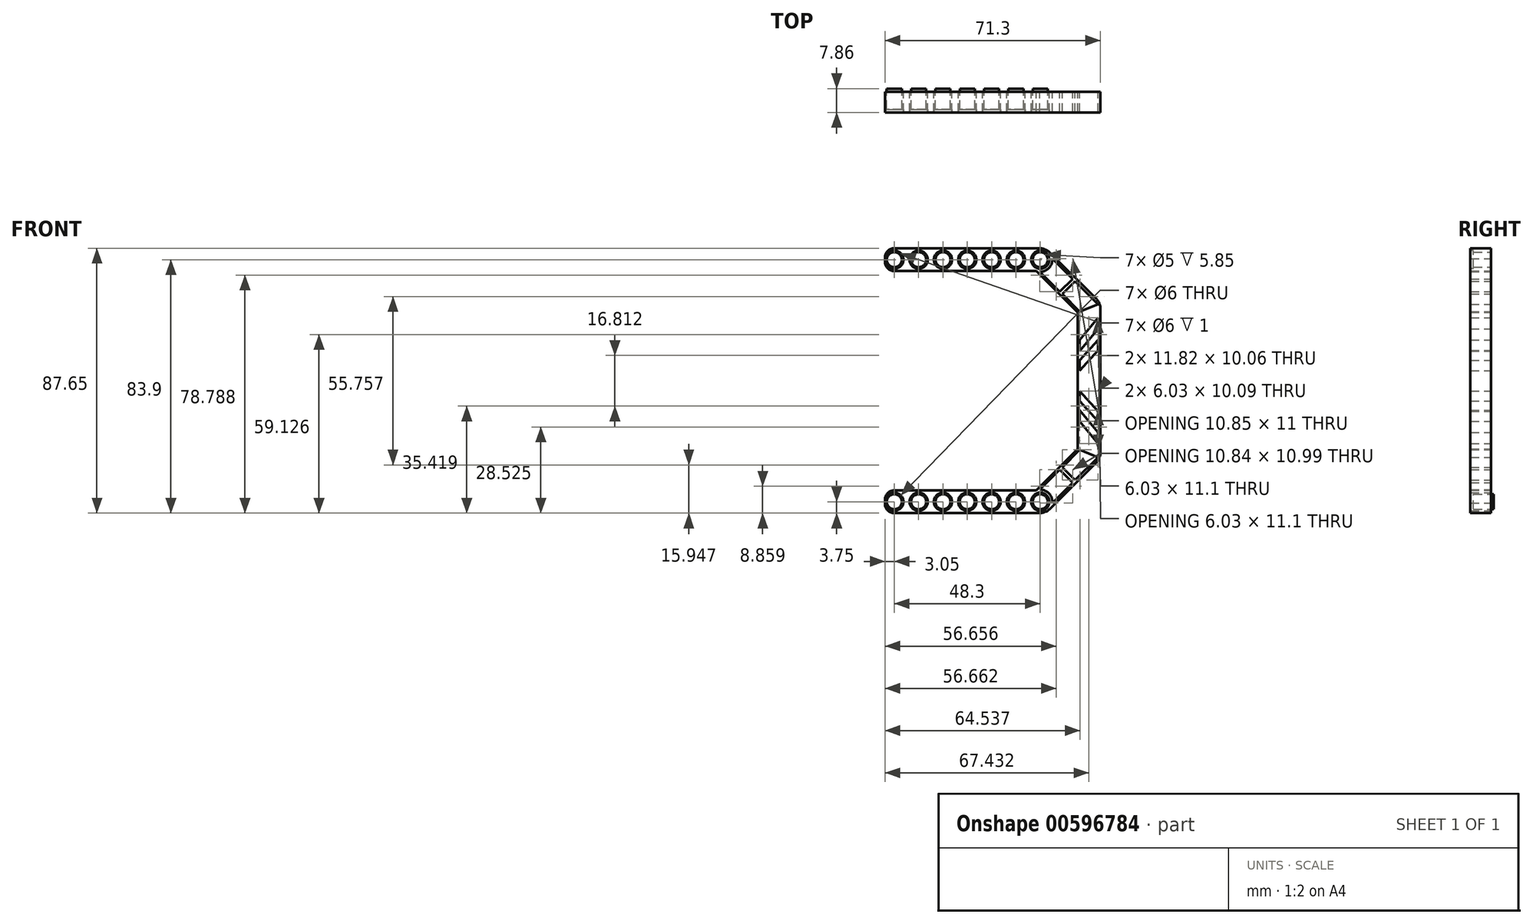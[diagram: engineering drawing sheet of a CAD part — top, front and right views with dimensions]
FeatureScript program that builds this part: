
annotation { "Feature Type Name" : "Feature", "Feature Type Description" : "" }
export const myFeature = defineFeature(function(context is Context, id is Id, definition is map)
    precondition{}
    {
        {
            var Q0;
            Q0=qCreatedBy(makeId("Front.planeOp"),FACE);
            var sketch = newSketch(context, id + "F0", { "sketchPlane" : qUnion([Q0])});
            skLineSegment(sketch, "E0.bottom", {"start": v(17.53, 19.75) * mm, "end": v(-35.65, 19.75) * mm});
            skLineSegment(sketch, "E0.right", {"start": v(-35.65, 19.75) * mm, "end": v(-35.65, 12.25) * mm});
            skPoint(sketch, "E0.middle", {"position": v(0, 0) * mm});
            skPoint(sketch, "E1.end.orphan", {"position": v(0, 37.73) * mm});
            skPoint(sketch, "E2.start.orphan", {"position": v(14.4, 19.75) * mm});
            skPoint(sketch, "E3.start.orphan", {"position": v(35.65, -1.5) * mm});
            skLineSegment(sketch, "E4", {"start": v(-35.65, 12.25) * mm, "end": v(14.4, 12.25) * mm});
            skLineSegment(sketch, "E5", {"start": v(-35.65, 19.75) * mm, "end": v(17.53, 19.75) * mm});
            skLineSegment(sketch, "E6", {"start": v(14.4, 12.25) * mm, "end": v(28.1, -1.5) * mm});
            skLineSegment(sketch, "E7", {"start": v(17.53, 19.75) * mm, "end": v(35.65, 1.63) * mm});
            skLineSegment(sketch, "E8.trimOffspring", {"start": v(28.1, -1.5) * mm, "end": v(28.15, -19.75) * mm});
            skPoint(sketch, "E9.start.orphan", {"position": v(21.25, 5.37) * mm});
            skPoint(sketch, "E10.trimOffspring.end.orphan", {"position": v(28.15, 12.2) * mm});
            skCircle(sketch, "E11", {"center": v(-16.5, 16) * mm, "radius": 2.5 * mm});
            skCircle(sketch, "E12", {"center": v(-24.55, 16) * mm, "radius": 2.5 * mm});
            skCircle(sketch, "E13", {"center": v(-32.6, 16) * mm, "radius": 2.5 * mm});
            skCircle(sketch, "E14", {"center": v(-8.45, 16) * mm, "radius": 2.5 * mm});
            skCircle(sketch, "E15", {"center": v(-0.4, 16) * mm, "radius": 2.5 * mm});
            skCircle(sketch, "E16", {"center": v(7.65, 16) * mm, "radius": 2.5 * mm});
            skCircle(sketch, "E17", {"center": v(15.7, 16) * mm, "radius": 2.5 * mm});
            skCircle(sketch, "E18", {"center": v(-32.6, 16) * mm, "radius": 3 * mm});
            skCircle(sketch, "E19", {"center": v(-24.55, 16) * mm, "radius": 3 * mm});
            skCircle(sketch, "E20", {"center": v(-16.5, 16) * mm, "radius": 3 * mm});
            skCircle(sketch, "E21", {"center": v(-8.45, 16) * mm, "radius": 3 * mm});
            skCircle(sketch, "E22", {"center": v(-0.4, 16) * mm, "radius": 3 * mm});
            skCircle(sketch, "E23", {"center": v(7.65, 16) * mm, "radius": 3 * mm});
            skCircle(sketch, "E24", {"center": v(15.7, 16) * mm, "radius": 3 * mm});
            skPoint(sketch, "E25.orphan", {"position": v(-35.65, -19.75) * mm});
            skLineSegment(sketch, "E26.trimOffspring", {"start": v(35.65, 1.63) * mm, "end": v(35.65, -19.75) * mm});
            skLineSegment(sketch, "E27.left", {"start": v(28.15, -19.75) * mm, "end": v(28.15, -28.4) * mm});
            skLineSegment(sketch, "E27.right", {"start": v(35.65, -19.75) * mm, "end": v(35.65, -28.4) * mm});
            skPoint(sketch, "E28.startSnap0", {"position": v(35.65, -24.07) * mm});
            skCircle(sketch, "E29.MirrorC", {"center": v(15.7, -64.15) * mm, "radius": 2.5 * mm});
            skLineSegment(sketch, "E30.MirrorCS", {"start": v(35.65, -67.9) * mm, "end": v(35.65, -66.58) * mm});
            skCircle(sketch, "E31.MirrorC", {"center": v(-0.4, -64.15) * mm, "radius": 2.5 * mm});
            skLineSegment(sketch, "E32.MirrorCS", {"start": v(-35.65, -67.9) * mm, "end": v(-35.65, -60.4) * mm});
            skCircle(sketch, "E33.MirrorC", {"center": v(-16.5, -64.15) * mm, "radius": 2.5 * mm});
            skLineSegment(sketch, "E34.MirrorCS", {"start": v(17.53, -67.9) * mm, "end": v(-35.65, -67.9) * mm});
            skPoint(sketch, "E35.MirrorP", {"position": v(-35.65, -28.4) * mm});
            skCircle(sketch, "E36.MirrorC", {"center": v(-8.45, -64.15) * mm, "radius": 2.5 * mm});
            skCircle(sketch, "E37.MirrorC", {"center": v(-24.55, -64.15) * mm, "radius": 2.5 * mm});
            skCircle(sketch, "E38.MirrorC", {"center": v(7.65, -64.15) * mm, "radius": 2.5 * mm});
            skCircle(sketch, "E39.MirrorC", {"center": v(-32.6, -64.15) * mm, "radius": 2.5 * mm});
            skCircle(sketch, "E40.MirrorC", {"center": v(-0.4, -64.15) * mm, "radius": 3 * mm});
            skPoint(sketch, "E41.MirrorP", {"position": v(21.25, -53.52) * mm});
            skCircle(sketch, "E42.MirrorC", {"center": v(-16.5, -64.15) * mm, "radius": 3 * mm});
            skCircle(sketch, "E43.MirrorC", {"center": v(-8.45, -64.15) * mm, "radius": 3 * mm});
            skCircle(sketch, "E44.MirrorC", {"center": v(7.65, -64.15) * mm, "radius": 3 * mm});
            skLineSegment(sketch, "E45.MirrorCS", {"start": v(28.1, -46.65) * mm, "end": v(28.15, -28.4) * mm});
            skCircle(sketch, "E46.MirrorC", {"center": v(-32.6, -64.15) * mm, "radius": 3 * mm});
            skLineSegment(sketch, "E47.MirrorCS", {"start": v(-35.65, -67.9) * mm, "end": v(17.53, -67.9) * mm});
            skLineSegment(sketch, "E48.MirrorCS", {"start": v(35.65, -49.78) * mm, "end": v(35.65, -28.4) * mm});
            skCircle(sketch, "E49.MirrorC", {"center": v(15.7, -64.15) * mm, "radius": 3 * mm});
            skPoint(sketch, "E50.MirrorP", {"position": v(0, -48.15) * mm});
            skLineSegment(sketch, "E51.MirrorCS", {"start": v(14.4, -60.4) * mm, "end": v(28.1, -46.65) * mm});
            skPoint(sketch, "E52.MirrorP", {"position": v(14.4, -67.9) * mm});
            skLineSegment(sketch, "E53.MirrorCS", {"start": v(-35.65, -60.4) * mm, "end": v(14.4, -60.4) * mm});
            skPoint(sketch, "E54.MirrorP", {"position": v(28.15, -60.35) * mm});
            skPoint(sketch, "E55.MirrorP", {"position": v(35.65, -46.65) * mm});
            skCircle(sketch, "E56.MirrorC", {"center": v(-24.55, -64.15) * mm, "radius": 3 * mm});
            skLineSegment(sketch, "E57", {"start": v(15.59, -60.15) * mm, "end": v(28.77, -46.93) * mm});
            skLineSegment(sketch, "E58", {"start": v(34.8, -49.42) * mm, "end": v(28.77, -46.93) * mm});
            skLineSegment(sketch, "E59.trimOffspring", {"start": v(19.68, -64.54) * mm, "end": v(34.8, -49.42) * mm});
            skLineSegment(sketch, "E60", {"start": v(15.59, 12) * mm, "end": v(28.77, -1.22) * mm});
            skLineSegment(sketch, "E61", {"start": v(34.8, 1.27) * mm, "end": v(28.77, -1.22) * mm});
            skLineSegment(sketch, "E62.trimOffspring", {"start": v(19.68, 16.39) * mm, "end": v(34.8, 1.27) * mm});
            skArc(sketch, "E63.trimOffspring", {"start": v(18.96, 18.32) * mm, "mid": v(18.92, 18.37) * mm, "end": v(18.88, 18.42) * mm});
            skArc(sketch, "E64.trimOffspring", {"start": v(15.59, 12) * mm, "mid": v(18.62, 13.27) * mm, "end": v(19.68, 16.39) * mm});
            skArc(sketch, "E65", {"start": v(18.88, -66.58) * mm, "mid": v(18.92, -66.52) * mm, "end": v(18.96, -66.47) * mm});
            skArc(sketch, "E66.trimOffspring", {"start": v(19.68, -64.54) * mm, "mid": v(18.62, -61.42) * mm, "end": v(15.59, -60.15) * mm});
            skPoint(sketch, "E67.bottom.end.orphan", {"position": v(35.65, -19.75) * mm});
            skPoint(sketch, "E68.MirrorCS.end.orphan", {"position": v(35.65, -28.4) * mm});
            skLineSegment(sketch, "E69", {"start": v(28.77, -10.62) * mm, "end": v(28.77, -10.63) * mm});
            skLineSegment(sketch, "E70", {"start": v(34.8, -44.93) * mm, "end": v(34.8, -41.23) * mm});
            skPoint(sketch, "E71.oppositeSnap0", {"position": v(28.13, -10.63) * mm});
            skLineSegment(sketch, "E71.top", {"start": v(28.77, -10.63) * mm, "end": v(28.77, -10.63) * mm});
            skLineSegment(sketch, "E71.left", {"start": v(28.77, -24.07) * mm, "end": v(28.77, -22.4) * mm});
            skPoint(sketch, "E72.oppositeSnap0", {"position": v(28.13, -37.52) * mm});
            skLineSegment(sketch, "E72.left", {"start": v(28.77, -24.07) * mm, "end": v(28.77, -25.76) * mm});
            skLineSegment(sketch, "E72.right", {"start": v(34.8, -27.44) * mm, "end": v(34.8, -30.8) * mm});
            skPoint(sketch, "E73.oppositeSnap0", {"position": v(34.8, -17.35) * mm});
            skLineSegment(sketch, "E73.left", {"start": v(34.8, -20.71) * mm, "end": v(34.8, -17.35) * mm});
            skLineSegment(sketch, "E74", {"start": v(28.77, -10.63) * mm, "end": v(34.8, -3.22) * mm});
            skLineSegment(sketch, "E75", {"start": v(28.77, -17.35) * mm, "end": v(34.8, -10.63) * mm});
            skLineSegment(sketch, "E76", {"start": v(30.28, -22.4) * mm, "end": v(34.8, -17.35) * mm});
            skLineSegment(sketch, "E77", {"start": v(31.78, -24.07) * mm, "end": v(34.8, -20.71) * mm});
            skPoint(sketch, "E78.orphan", {"position": v(37.8, -17.35) * mm});
            skLineSegment(sketch, "E79", {"start": v(30.28, -25.76) * mm, "end": v(34.8, -30.8) * mm});
            skLineSegment(sketch, "E80", {"start": v(31.78, -24.07) * mm, "end": v(34.8, -27.44) * mm});
            skPoint(sketch, "E81.orphan", {"position": v(37.8, -30.8) * mm});
            skPoint(sketch, "E82.startSnap0", {"position": v(31.78, 0.02) * mm});
            skLineSegment(sketch, "E83.trimOffspring", {"start": v(28.77, -17.35) * mm, "end": v(28.77, -20.71) * mm});
            skLineSegment(sketch, "E84", {"start": v(28.77, -10.63) * mm, "end": v(28.77, -14.32) * mm});
            skLineSegment(sketch, "E85", {"start": v(34.8, -6.92) * mm, "end": v(34.8, -3.22) * mm});
            skLineSegment(sketch, "E86", {"start": v(28.77, -41.23) * mm, "end": v(28.77, -41.22) * mm});
            skLineSegment(sketch, "E87", {"start": v(27.24, -56.98) * mm, "end": v(22.98, -52.74) * mm});
            skLineSegment(sketch, "E88", {"start": v(27.24, 8.83) * mm, "end": v(22.98, 4.59) * mm});
            skLineSegment(sketch, "E89", {"start": v(22.18, 5.39) * mm, "end": v(26.44, 9.63) * mm});
            skLineSegment(sketch, "E90", {"start": v(22.17, -53.54) * mm, "end": v(26.42, -57.8) * mm});
            skPoint(sketch, "E91.orphan", {"position": v(19.35, -50.72) * mm});
            skLineSegment(sketch, "E92.MirrorCS", {"start": v(28.77, -30.8) * mm, "end": v(34.8, -37.52) * mm});
            skLineSegment(sketch, "E93.MirrorCS", {"start": v(28.77, -37.52) * mm, "end": v(34.8, -44.93) * mm});
            skLineSegment(sketch, "E94", {"start": v(34.8, -44.93) * mm, "end": v(28.77, -37.53) * mm});
            skLineSegment(sketch, "E95", {"start": v(28.77, -22.4) * mm, "end": v(28.77, -24.07) * mm});
            skLineSegment(sketch, "E96", {"start": v(28.77, -22.4) * mm, "end": v(30.28, -22.4) * mm});
            skLineSegment(sketch, "E97", {"start": v(30.28, -25.76) * mm, "end": v(28.77, -25.76) * mm});
            skLineSegment(sketch, "E98", {"start": v(34.8, -13.99) * mm, "end": v(28.77, -20.71) * mm});
            skLineSegment(sketch, "E99", {"start": v(34.8, -6.92) * mm, "end": v(28.77, -14.32) * mm});
            skLineSegment(sketch, "E100", {"start": v(28.77, -33.82) * mm, "end": v(34.8, -41.23) * mm});
            skLineSegment(sketch, "E101", {"start": v(34.8, -34.16) * mm, "end": v(34.8, -37.52) * mm, "construction": true});
            skLineSegment(sketch, "E102", {"start": v(34.8, -34.16) * mm, "end": v(28.77, -27.44) * mm});
            skPoint(sketch, "E82.start.orphan", {"position": v(31.78, -3.22) * mm});
            skPoint(sketch, "E103.orphan", {"position": v(28.77, -14.33) * mm});
            skLineSegment(sketch, "E104.trimOffspring", {"start": v(34.8, -13.99) * mm, "end": v(34.8, -10.63) * mm});
            skLineSegment(sketch, "E105.trimOffspring", {"start": v(28.77, -20.71) * mm, "end": v(28.77, -17.35) * mm});
            skLineSegment(sketch, "E106.trimOffspring", {"start": v(28.77, -22.4) * mm, "end": v(28.77, -25.76) * mm});
            skPoint(sketch, "E107.orphan", {"position": v(34.8, -24.07) * mm});
            skLineSegment(sketch, "E108.trimOffspring", {"start": v(28.77, -27.44) * mm, "end": v(28.77, -30.8) * mm});
            skLineSegment(sketch, "E109.trimOffspring", {"start": v(34.8, -34.16) * mm, "end": v(34.8, -37.52) * mm});
            skLineSegment(sketch, "E110.trimOffspring", {"start": v(34.8, -30.8) * mm, "end": v(34.8, -27.44) * mm});
            skLineSegment(sketch, "E111.trimOffspring", {"start": v(28.77, -33.82) * mm, "end": v(28.77, -37.53) * mm});
            skLineSegment(sketch, "E112.trimOffspring", {"start": v(34.8, -37.52) * mm, "end": v(34.8, -34.16) * mm});
            skPoint(sketch, "E113.MirrorCS.end.orphan", {"position": v(28.77, -41.23) * mm});
            skPoint(sketch, "E113.MirrorCS.start.orphan", {"position": v(31.78, -44.93) * mm});
            skLineSegment(sketch, "E114", {"start": v(17.53, -67.9) * mm, "end": v(35.65, -49.78) * mm});
            skSolve(sketch);
        }
        {
            var Q0;
            {var subQ0=sQuery(id+"F0.wireOp",EDGE,"E88");Q0=makeQuery(id+"F0.imprint","IMPRINT",FACE,{"disambiguationData":[TD([[makeQuery(id+"F0.imprint","IMPRINT",EDGE,{"derivedFrom":subQ0}),-1.0]])]});}
            var Q1;
            {var subQ0=sQuery(id+"F0.wireOp",EDGE,"E87");Q1=makeQuery(id+"F0.imprint","IMPRINT",FACE,{"disambiguationData":[TD([[makeQuery(id+"F0.imprint","IMPRINT",EDGE,{"derivedFrom":subQ0}),1.0]])]});}
            var Q2;
            Q2=makeQuery(id+"F0.imprint","IMPRINT",FACE,{"disambiguationData":[TD([[makeQuery(id+"F0.imprint","IMPRINT",EDGE,{"derivedFrom":sQuery(id+"F0.wireOp",EDGE,"E13")}),-1.0]])]});
            var Q3;
            Q3=makeQuery(id+"F0.imprint","IMPRINT",FACE,{"disambiguationData":[TD([[makeQuery(id+"F0.imprint","IMPRINT",EDGE,{"derivedFrom":sQuery(id+"F0.wireOp",EDGE,"E12")}),-1.0]])]});
            var Q4;
            Q4=makeQuery(id+"F0.imprint","IMPRINT",FACE,{"disambiguationData":[TD([[makeQuery(id+"F0.imprint","IMPRINT",EDGE,{"derivedFrom":sQuery(id+"F0.wireOp",EDGE,"E11")}),-1.0]])]});
            var Q5;
            Q5=makeQuery(id+"F0.imprint","IMPRINT",FACE,{"disambiguationData":[TD([[makeQuery(id+"F0.imprint","IMPRINT",EDGE,{"derivedFrom":sQuery(id+"F0.wireOp",EDGE,"E15")}),-1.0]])]});
            var Q6;
            Q6=makeQuery(id+"F0.imprint","IMPRINT",FACE,{"disambiguationData":[TD([[makeQuery(id+"F0.imprint","IMPRINT",EDGE,{"derivedFrom":sQuery(id+"F0.wireOp",EDGE,"E16")}),-1.0]])]});
            var Q7;
            Q7=makeQuery(id+"F0.imprint","IMPRINT",FACE,{"disambiguationData":[TD([[makeQuery(id+"F0.imprint","IMPRINT",EDGE,{"derivedFrom":sQuery(id+"F0.wireOp",EDGE,"E14")}),-1.0]])]});
            var Q8;
            Q8=makeQuery(id+"F0.imprint","IMPRINT",FACE,{"disambiguationData":[TD([[makeQuery(id+"F0.imprint","IMPRINT",EDGE,{"derivedFrom":sQuery(id+"F0.wireOp",EDGE,"E17")}),-1.0]])]});
            var Q9;
            Q9=makeQuery(id+"F0.imprint","IMPRINT",FACE,{"disambiguationData":[TD([[makeQuery(id+"F0.imprint","IMPRINT",EDGE,{"derivedFrom":sQuery(id+"F0.wireOp",EDGE,"E38.MirrorC")}),1.0]])]});
            var Q10;
            Q10=makeQuery(id+"F0.imprint","IMPRINT",FACE,{"disambiguationData":[TD([[makeQuery(id+"F0.imprint","IMPRINT",EDGE,{"derivedFrom":sQuery(id+"F0.wireOp",EDGE,"E0.right")}),1.0]])]});
            var Q11;
            Q11=makeQuery(id+"F0.imprint","IMPRINT",FACE,{"disambiguationData":[TD([[makeQuery(id+"F0.imprint","IMPRINT",EDGE,{"derivedFrom":sQuery(id+"F0.wireOp",EDGE,"E29.MirrorC")}),1.0]])]});
            var Q12;
            Q12=makeQuery(id+"F0.imprint","IMPRINT",FACE,{"disambiguationData":[TD([[makeQuery(id+"F0.imprint","IMPRINT",EDGE,{"derivedFrom":sQuery(id+"F0.wireOp",EDGE,"E31.MirrorC")}),1.0]])]});
            var Q13;
            Q13=makeQuery(id+"F0.imprint","IMPRINT",FACE,{"disambiguationData":[TD([[makeQuery(id+"F0.imprint","IMPRINT",EDGE,{"derivedFrom":sQuery(id+"F0.wireOp",EDGE,"E36.MirrorC")}),1.0]])]});
            var Q14;
            Q14=makeQuery(id+"F0.imprint","IMPRINT",FACE,{"disambiguationData":[TD([[makeQuery(id+"F0.imprint","IMPRINT",EDGE,{"derivedFrom":sQuery(id+"F0.wireOp",EDGE,"E33.MirrorC")}),1.0]])]});
            var Q15;
            Q15=makeQuery(id+"F0.imprint","IMPRINT",FACE,{"disambiguationData":[TD([[makeQuery(id+"F0.imprint","IMPRINT",EDGE,{"derivedFrom":sQuery(id+"F0.wireOp",EDGE,"E37.MirrorC")}),1.0]])]});
            var Q16;
            Q16=makeQuery(id+"F0.imprint","IMPRINT",FACE,{"disambiguationData":[TD([[makeQuery(id+"F0.imprint","IMPRINT",EDGE,{"derivedFrom":sQuery(id+"F0.wireOp",EDGE,"E39.MirrorC")}),1.0]])]});
            extrude(context, id + "F1", {"entities" : qUnion([Q0, Q1, Q2, Q3, Q4, Q5, Q6, Q7, Q8, Q9, Q10, Q11, Q12, Q13, Q14, Q15, Q16]), "endBound" : BoundingType.SYMMETRIC, "depth" : 7.85 * mm, "offsetDistance" : 25 * mm});
        }
        {
            var Q0;
            Q0=makeQuery(id+"F1.opExtrude","SWEPT_EDGE",EDGE,{"disambiguationData":[OSD([sQuery(id+"F0.wireOp",EDGE,"E0.right"),sQuery(id+"F0.wireOp",EDGE,"E5")])]});
            var Q1;
            Q1=makeQuery(id+"F1.opExtrude","SWEPT_EDGE",EDGE,{"disambiguationData":[OSD([sQuery(id+"F0.wireOp",EDGE,"E0.right"),sQuery(id+"F0.wireOp",EDGE,"E4")])]});
            var Q2;
            Q2=makeQuery(id+"F1.opExtrude","SWEPT_EDGE",EDGE,{"disambiguationData":[OSD([sQuery(id+"F0.wireOp",EDGE,"E32.MirrorCS"),sQuery(id+"F0.wireOp",EDGE,"E53.MirrorCS")])]});
            var Q3;
            Q3=makeQuery(id+"F1.opExtrude","SWEPT_EDGE",EDGE,{"disambiguationData":[OSD([sQuery(id+"F0.wireOp",EDGE,"E32.MirrorCS"),sQuery(id+"F0.wireOp",EDGE,"E47.MirrorCS")])]});
            fillet(context, id + "F2", {"entities" : qUnion([Q0, Q1, Q2, Q3]), "radius" : 3 * mm, "tangentPropagation" : true, "allowEdgeOverflow" : false});
        }
        {
            var Q0;
            Q0=makeQuery(id+"F1.opExtrude","SWEPT_EDGE",EDGE,{"disambiguationData":[OSD([sQuery(id+"F0.wireOp",EDGE,"E7"),sQuery(id+"F0.wireOp",EDGE,"E26.trimOffspring")])]});
            var Q1;
            Q1=makeQuery(id+"F1.opExtrude","SWEPT_EDGE",EDGE,{"disambiguationData":[OSD([sQuery(id+"F0.wireOp",EDGE,"E5"),sQuery(id+"F0.wireOp",EDGE,"E7")])]});
            var Q2;
            Q2=makeQuery(id+"F1.opExtrude","SWEPT_EDGE",EDGE,{"disambiguationData":[OSD([sQuery(id+"F0.wireOp",EDGE,"E48.MirrorCS"),sQuery(id+"F0.wireOp",EDGE,"E114")])]});
            var Q3;
            Q3=makeQuery(id+"F1.opExtrude","SWEPT_EDGE",EDGE,{"disambiguationData":[OSD([sQuery(id+"F0.wireOp",EDGE,"E47.MirrorCS"),sQuery(id+"F0.wireOp",EDGE,"E114")])]});
            fillet(context, id + "F3", {"entities" : qUnion([Q0, Q1, Q2, Q3]), "radius" : 5 * mm, "tangentPropagation" : true, "allowEdgeOverflow" : false});
        }
        {
            var Q0;
            Q0=makeQuery(id+"F1.opExtrude","CAP_FACE",FACE,{"disambiguationData":[OSD([sQuery(id+"F0.wireOp",EDGE,"E0.right"),sQuery(id+"F0.wireOp",EDGE,"E4"),sQuery(id+"F0.wireOp",EDGE,"E5"),sQuery(id+"F0.wireOp",EDGE,"E6"),sQuery(id+"F0.wireOp",EDGE,"E7"),sQuery(id+"F0.wireOp",EDGE,"E8.trimOffspring"),sQuery(id+"F0.wireOp",EDGE,"E11"),sQuery(id+"F0.wireOp",EDGE,"E12"),sQuery(id+"F0.wireOp",EDGE,"E13"),sQuery(id+"F0.wireOp",EDGE,"E14"),sQuery(id+"F0.wireOp",EDGE,"E15"),sQuery(id+"F0.wireOp",EDGE,"E16"),sQuery(id+"F0.wireOp",EDGE,"E17"),sQuery(id+"F0.wireOp",EDGE,"E26.trimOffspring"),sQuery(id+"F0.wireOp",EDGE,"E27.left"),sQuery(id+"F0.wireOp",EDGE,"E27.right"),sQuery(id+"F0.wireOp",EDGE,"E29.MirrorC"),sQuery(id+"F0.wireOp",EDGE,"E31.MirrorC"),sQuery(id+"F0.wireOp",EDGE,"E33.MirrorC"),sQuery(id+"F0.wireOp",EDGE,"E32.MirrorCS"),sQuery(id+"F0.wireOp",EDGE,"E36.MirrorC"),sQuery(id+"F0.wireOp",EDGE,"E37.MirrorC"),sQuery(id+"F0.wireOp",EDGE,"E38.MirrorC"),sQuery(id+"F0.wireOp",EDGE,"E39.MirrorC"),sQuery(id+"F0.wireOp",EDGE,"E45.MirrorCS"),sQuery(id+"F0.wireOp",EDGE,"E47.MirrorCS"),sQuery(id+"F0.wireOp",EDGE,"E48.MirrorCS"),sQuery(id+"F0.wireOp",EDGE,"E51.MirrorCS"),sQuery(id+"F0.wireOp",EDGE,"E53.MirrorCS"),sQuery(id+"F0.wireOp",EDGE,"E57"),sQuery(id+"F0.wireOp",EDGE,"E58"),sQuery(id+"F0.wireOp",EDGE,"E59.trimOffspring"),sQuery(id+"F0.wireOp",EDGE,"E60"),sQuery(id+"F0.wireOp",EDGE,"E61"),sQuery(id+"F0.wireOp",EDGE,"E62.trimOffspring"),sQuery(id+"F0.wireOp",EDGE,"E64.trimOffspring"),sQuery(id+"F0.wireOp",EDGE,"E66.trimOffspring"),sQuery(id+"F0.wireOp",EDGE,"E70"),sQuery(id+"F0.wireOp",EDGE,"E71.top"),sQuery(id+"F0.wireOp",EDGE,"E74"),sQuery(id+"F0.wireOp",EDGE,"E75"),sQuery(id+"F0.wireOp",EDGE,"E84"),sQuery(id+"F0.wireOp",EDGE,"E85"),sQuery(id+"F0.wireOp",EDGE,"E87"),sQuery(id+"F0.wireOp",EDGE,"E88"),sQuery(id+"F0.wireOp",EDGE,"E89"),sQuery(id+"F0.wireOp",EDGE,"E90"),sQuery(id+"F0.wireOp",EDGE,"E92.MirrorCS"),sQuery(id+"F0.wireOp",EDGE,"E94"),sQuery(id+"F0.wireOp",EDGE,"E98"),sQuery(id+"F0.wireOp",EDGE,"E99"),sQuery(id+"F0.wireOp",EDGE,"E100"),sQuery(id+"F0.wireOp",EDGE,"E102"),sQuery(id+"F0.wireOp",EDGE,"E104.trimOffspring"),sQuery(id+"F0.wireOp",EDGE,"E105.trimOffspring"),sQuery(id+"F0.wireOp",EDGE,"E108.trimOffspring"),sQuery(id+"F0.wireOp",EDGE,"E111.trimOffspring"),sQuery(id+"F0.wireOp",EDGE,"E112.trimOffspring"),sQuery(id+"F0.wireOp",EDGE,"E114")])],"isStart":false});
            var sketch = newSketch(context, id + "F4", { "sketchPlane" : qUnion([Q0])});
            skCircle(sketch, "E115", {"center": v(-24.55, 16) * mm, "radius": 3 * mm});
            skCircle(sketch, "E116", {"center": v(-16.5, 16) * mm, "radius": 3 * mm});
            skCircle(sketch, "E117", {"center": v(-8.45, 16) * mm, "radius": 3 * mm});
            skCircle(sketch, "E118", {"center": v(-0.4, 16) * mm, "radius": 3 * mm});
            skCircle(sketch, "E119", {"center": v(7.65, 16) * mm, "radius": 3 * mm});
            skCircle(sketch, "E120", {"center": v(15.7, 16) * mm, "radius": 3 * mm});
            skCircle(sketch, "E121", {"center": v(-32.6, 16) * mm, "radius": 3 * mm});
            skCircle(sketch, "E122", {"center": v(-32.6, -64.15) * mm, "radius": 3 * mm});
            skCircle(sketch, "E123", {"center": v(-24.55, -64.15) * mm, "radius": 3 * mm});
            skCircle(sketch, "E124", {"center": v(-16.5, -64.15) * mm, "radius": 3 * mm});
            skCircle(sketch, "E125", {"center": v(-8.45, -64.15) * mm, "radius": 3 * mm});
            skCircle(sketch, "E126", {"center": v(-0.4, -64.15) * mm, "radius": 3 * mm});
            skCircle(sketch, "E127", {"center": v(7.65, -64.15) * mm, "radius": 3 * mm});
            skCircle(sketch, "E128", {"center": v(15.7, -64.15) * mm, "radius": 3 * mm});
            skSolve(sketch);
        }
        {
            var Q0;
            Q0=qSketchRegion(id+"F4",true);
            extrude(context, id + "F5", {"entities" : qUnion([Q0]), "operationType" : NewBodyOperationType.REMOVE, "oppositeDirection" : true, "depth" : 1 * mm, "offsetDistance" : 25 * mm});
        }
        {
            var Q0;
            Q0=makeQuery(id+"F1.opExtrude","CAP_FACE",FACE,{"disambiguationData":[OSD([sQuery(id+"F0.wireOp",EDGE,"E0.right"),sQuery(id+"F0.wireOp",EDGE,"E4"),sQuery(id+"F0.wireOp",EDGE,"E5"),sQuery(id+"F0.wireOp",EDGE,"E6"),sQuery(id+"F0.wireOp",EDGE,"E7"),sQuery(id+"F0.wireOp",EDGE,"E8.trimOffspring"),sQuery(id+"F0.wireOp",EDGE,"E11"),sQuery(id+"F0.wireOp",EDGE,"E12"),sQuery(id+"F0.wireOp",EDGE,"E13"),sQuery(id+"F0.wireOp",EDGE,"E14"),sQuery(id+"F0.wireOp",EDGE,"E15"),sQuery(id+"F0.wireOp",EDGE,"E16"),sQuery(id+"F0.wireOp",EDGE,"E17"),sQuery(id+"F0.wireOp",EDGE,"E26.trimOffspring"),sQuery(id+"F0.wireOp",EDGE,"E27.left"),sQuery(id+"F0.wireOp",EDGE,"E27.right"),sQuery(id+"F0.wireOp",EDGE,"E29.MirrorC"),sQuery(id+"F0.wireOp",EDGE,"E31.MirrorC"),sQuery(id+"F0.wireOp",EDGE,"E33.MirrorC"),sQuery(id+"F0.wireOp",EDGE,"E32.MirrorCS"),sQuery(id+"F0.wireOp",EDGE,"E36.MirrorC"),sQuery(id+"F0.wireOp",EDGE,"E37.MirrorC"),sQuery(id+"F0.wireOp",EDGE,"E38.MirrorC"),sQuery(id+"F0.wireOp",EDGE,"E39.MirrorC"),sQuery(id+"F0.wireOp",EDGE,"E45.MirrorCS"),sQuery(id+"F0.wireOp",EDGE,"E47.MirrorCS"),sQuery(id+"F0.wireOp",EDGE,"E48.MirrorCS"),sQuery(id+"F0.wireOp",EDGE,"E51.MirrorCS"),sQuery(id+"F0.wireOp",EDGE,"E53.MirrorCS"),sQuery(id+"F0.wireOp",EDGE,"E57"),sQuery(id+"F0.wireOp",EDGE,"E58"),sQuery(id+"F0.wireOp",EDGE,"E59.trimOffspring"),sQuery(id+"F0.wireOp",EDGE,"E60"),sQuery(id+"F0.wireOp",EDGE,"E61"),sQuery(id+"F0.wireOp",EDGE,"E62.trimOffspring"),sQuery(id+"F0.wireOp",EDGE,"E64.trimOffspring"),sQuery(id+"F0.wireOp",EDGE,"E66.trimOffspring"),sQuery(id+"F0.wireOp",EDGE,"E70"),sQuery(id+"F0.wireOp",EDGE,"E71.top"),sQuery(id+"F0.wireOp",EDGE,"E74"),sQuery(id+"F0.wireOp",EDGE,"E75"),sQuery(id+"F0.wireOp",EDGE,"E84"),sQuery(id+"F0.wireOp",EDGE,"E85"),sQuery(id+"F0.wireOp",EDGE,"E87"),sQuery(id+"F0.wireOp",EDGE,"E88"),sQuery(id+"F0.wireOp",EDGE,"E89"),sQuery(id+"F0.wireOp",EDGE,"E90"),sQuery(id+"F0.wireOp",EDGE,"E92.MirrorCS"),sQuery(id+"F0.wireOp",EDGE,"E94"),sQuery(id+"F0.wireOp",EDGE,"E98"),sQuery(id+"F0.wireOp",EDGE,"E99"),sQuery(id+"F0.wireOp",EDGE,"E100"),sQuery(id+"F0.wireOp",EDGE,"E102"),sQuery(id+"F0.wireOp",EDGE,"E104.trimOffspring"),sQuery(id+"F0.wireOp",EDGE,"E105.trimOffspring"),sQuery(id+"F0.wireOp",EDGE,"E108.trimOffspring"),sQuery(id+"F0.wireOp",EDGE,"E111.trimOffspring"),sQuery(id+"F0.wireOp",EDGE,"E112.trimOffspring"),sQuery(id+"F0.wireOp",EDGE,"E114")])],"isStart":true});
            var sketch = newSketch(context, id + "F6", { "sketchPlane" : qUnion([Q0])});
            skCircle(sketch, "E129", {"center": v(-15.7, 16) * mm, "radius": 3 * mm});
            skCircle(sketch, "E130", {"center": v(-7.65, 16) * mm, "radius": 3 * mm});
            skCircle(sketch, "E131", {"center": v(0.4, 16) * mm, "radius": 3 * mm});
            skCircle(sketch, "E132", {"center": v(8.45, 16) * mm, "radius": 3 * mm});
            skCircle(sketch, "E133", {"center": v(16.5, 16) * mm, "radius": 3 * mm});
            skCircle(sketch, "E134", {"center": v(24.55, 16) * mm, "radius": 3 * mm});
            skCircle(sketch, "E135", {"center": v(32.6, 16) * mm, "radius": 3 * mm});
            skCircle(sketch, "E136", {"center": v(-15.7, -64.15) * mm, "radius": 3 * mm});
            skCircle(sketch, "E137", {"center": v(-7.65, -64.15) * mm, "radius": 3 * mm});
            skCircle(sketch, "E138", {"center": v(0.4, -64.15) * mm, "radius": 3 * mm});
            skCircle(sketch, "E139", {"center": v(8.45, -64.15) * mm, "radius": 3 * mm});
            skCircle(sketch, "E140", {"center": v(16.5, -64.15) * mm, "radius": 3 * mm});
            skCircle(sketch, "E141", {"center": v(24.55, -64.15) * mm, "radius": 3 * mm});
            skCircle(sketch, "E142", {"center": v(32.6, -64.15) * mm, "radius": 3 * mm});
            skSolve(sketch);
        }
        {
            var Q0;
            Q0=makeQuery(id+"F6.imprint","IMPRINT",FACE,{"disambiguationData":[TD([[makeQuery(id+"F6.imprint","IMPRINT",EDGE,{"derivedFrom":sQuery(id+"F6.wireOp",EDGE,"E129")}),1.0]])]});
            var Q1;
            Q1=makeQuery(id+"F6.imprint","IMPRINT",FACE,{"disambiguationData":[TD([[makeQuery(id+"F6.imprint","IMPRINT",EDGE,{"derivedFrom":sQuery(id+"F6.wireOp",EDGE,"E130")}),1.0]])]});
            var Q2;
            Q2=makeQuery(id+"F6.imprint","IMPRINT",FACE,{"disambiguationData":[TD([[makeQuery(id+"F6.imprint","IMPRINT",EDGE,{"derivedFrom":sQuery(id+"F6.wireOp",EDGE,"E131")}),1.0]])]});
            var Q3;
            Q3=makeQuery(id+"F6.imprint","IMPRINT",FACE,{"disambiguationData":[TD([[makeQuery(id+"F6.imprint","IMPRINT",EDGE,{"derivedFrom":sQuery(id+"F6.wireOp",EDGE,"E132")}),1.0]])]});
            var Q4;
            Q4=makeQuery(id+"F6.imprint","IMPRINT",FACE,{"disambiguationData":[TD([[makeQuery(id+"F6.imprint","IMPRINT",EDGE,{"derivedFrom":sQuery(id+"F6.wireOp",EDGE,"E133")}),1.0]])]});
            var Q5;
            Q5=makeQuery(id+"F6.imprint","IMPRINT",FACE,{"disambiguationData":[TD([[makeQuery(id+"F6.imprint","IMPRINT",EDGE,{"derivedFrom":sQuery(id+"F6.wireOp",EDGE,"E134")}),1.0]])]});
            var Q6;
            Q6=makeQuery(id+"F6.imprint","IMPRINT",FACE,{"disambiguationData":[TD([[makeQuery(id+"F6.imprint","IMPRINT",EDGE,{"derivedFrom":sQuery(id+"F6.wireOp",EDGE,"E135")}),1.0]])]});
            var Q7;
            Q7=makeQuery(id+"F6.imprint","IMPRINT",FACE,{"disambiguationData":[TD([[makeQuery(id+"F6.imprint","IMPRINT",EDGE,{"derivedFrom":sQuery(id+"F6.wireOp",EDGE,"E136")}),1.0]])]});
            var Q8;
            Q8=makeQuery(id+"F6.imprint","IMPRINT",FACE,{"disambiguationData":[TD([[makeQuery(id+"F6.imprint","IMPRINT",EDGE,{"derivedFrom":sQuery(id+"F6.wireOp",EDGE,"E137")}),1.0]])]});
            var Q9;
            Q9=makeQuery(id+"F6.imprint","IMPRINT",FACE,{"disambiguationData":[TD([[makeQuery(id+"F6.imprint","IMPRINT",EDGE,{"derivedFrom":sQuery(id+"F6.wireOp",EDGE,"E138")}),1.0]])]});
            var Q10;
            Q10=makeQuery(id+"F6.imprint","IMPRINT",FACE,{"disambiguationData":[TD([[makeQuery(id+"F6.imprint","IMPRINT",EDGE,{"derivedFrom":sQuery(id+"F6.wireOp",EDGE,"E139")}),1.0]])]});
            var Q11;
            Q11=makeQuery(id+"F6.imprint","IMPRINT",FACE,{"disambiguationData":[TD([[makeQuery(id+"F6.imprint","IMPRINT",EDGE,{"derivedFrom":sQuery(id+"F6.wireOp",EDGE,"E140")}),1.0]])]});
            var Q12;
            Q12=makeQuery(id+"F6.imprint","IMPRINT",FACE,{"disambiguationData":[TD([[makeQuery(id+"F6.imprint","IMPRINT",EDGE,{"derivedFrom":sQuery(id+"F6.wireOp",EDGE,"E141")}),1.0]])]});
            var Q13;
            Q13=makeQuery(id+"F6.imprint","IMPRINT",FACE,{"disambiguationData":[TD([[makeQuery(id+"F6.imprint","IMPRINT",EDGE,{"derivedFrom":sQuery(id+"F6.wireOp",EDGE,"E142")}),1.0]])]});
            extrude(context, id + "F7", {"entities" : qUnion([Q0, Q1, Q2, Q3, Q4, Q5, Q6, Q7, Q8, Q9, Q10, Q11, Q12, Q13]), "operationType" : NewBodyOperationType.REMOVE, "oppositeDirection" : true, "depth" : 1 * mm, "offsetDistance" : 25 * mm});
        }
    });
